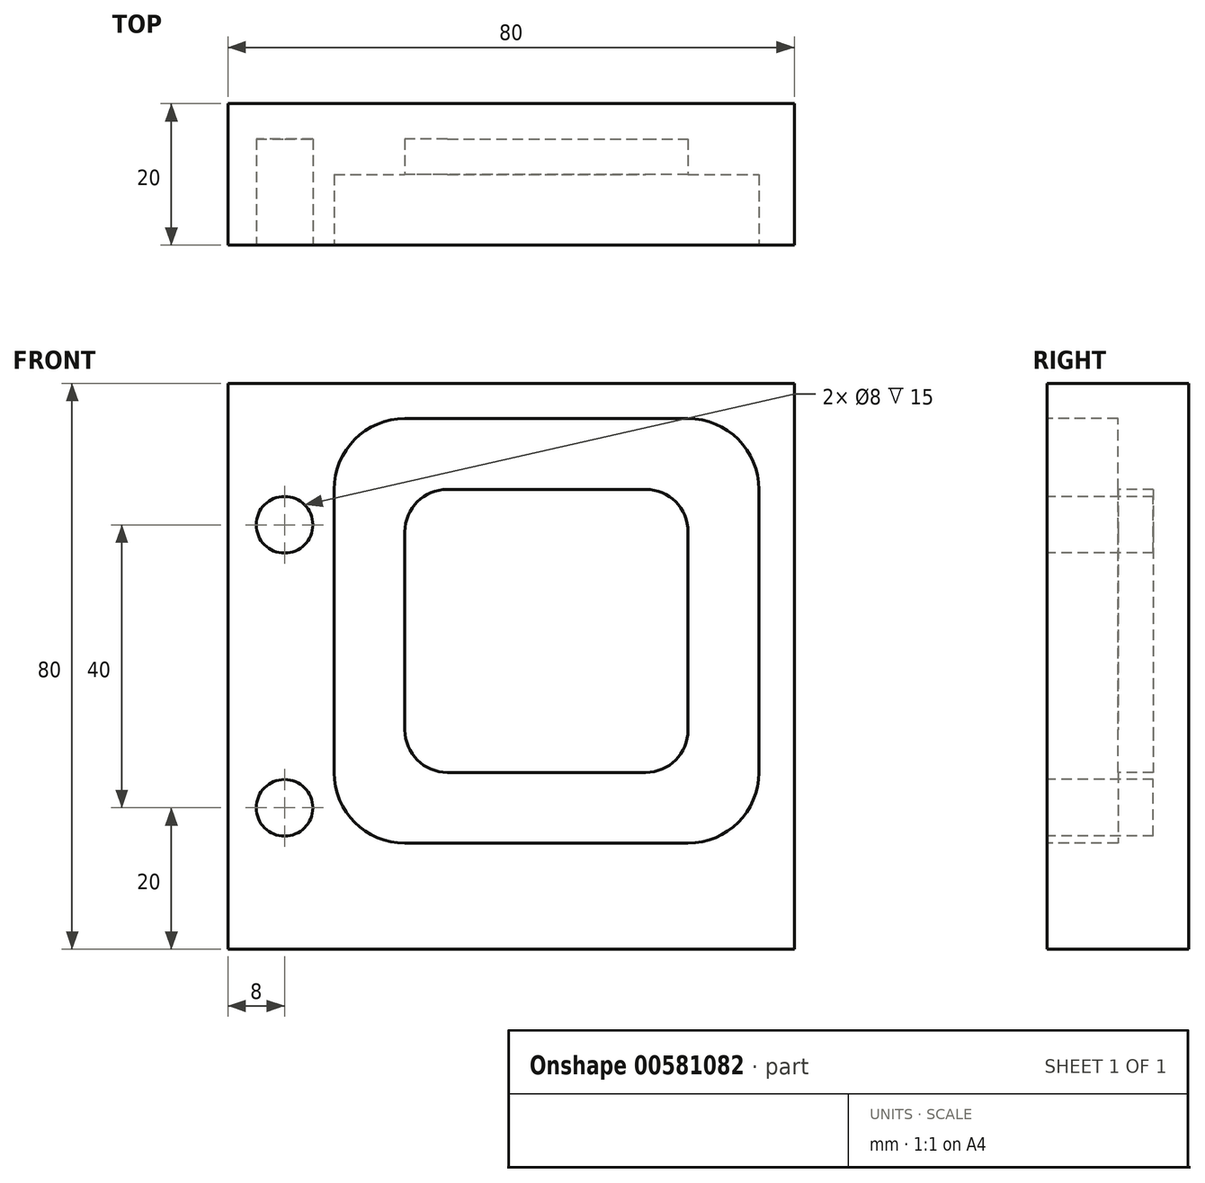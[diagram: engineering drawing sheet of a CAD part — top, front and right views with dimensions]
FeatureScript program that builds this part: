
annotation { "Feature Type Name" : "Feature", "Feature Type Description" : "" }
export const myFeature = defineFeature(function(context is Context, id is Id, definition is map)
    precondition{}
    {
        {
            var Q0;
            Q0=qCreatedBy(makeId("Front.planeOp"),FACE);
            var sketch = newSketch(context, id + "F0", { "sketchPlane" : qUnion([Q0])});
            skLineSegment(sketch, "E0.bottom", {"start": v(-40, 40) * mm, "end": v(40, 40) * mm});
            skLineSegment(sketch, "E0.top", {"start": v(-40, -40) * mm, "end": v(40, -40) * mm});
            skLineSegment(sketch, "E0.left", {"start": v(-40, 40) * mm, "end": v(-40, -40) * mm});
            skLineSegment(sketch, "E0.right", {"start": v(40, 40) * mm, "end": v(40, -40) * mm});
            skPoint(sketch, "E0.middle", {"position": v(0, 0) * mm});
            skSolve(sketch);
        }
        {
            var Q0;
            Q0=makeQuery(id+"F0.imprint","IMPRINT",FACE,{"disambiguationData":[TD([[makeQuery(id+"F0.imprint","IMPRINT",EDGE,{"derivedFrom":sQuery(id+"F0.wireOp",EDGE,"E0.bottom")}),-1.0]])]});
            extrude(context, id + "F1", {"entities" : qUnion([Q0]), "depth" : 20 * mm, "offsetDistance" : 25 * mm});
        }
        {
            var Q0;
            Q0=makeQuery(id+"F1.opExtrude","CAP_FACE",FACE,{"disambiguationData":[OSD([sQuery(id+"F0.wireOp",EDGE,"E0.bottom"),sQuery(id+"F0.wireOp",EDGE,"E0.top"),sQuery(id+"F0.wireOp",EDGE,"E0.left"),sQuery(id+"F0.wireOp",EDGE,"E0.right")])],"isStart":false});
            var sketch = newSketch(context, id + "F2", { "sketchPlane" : qUnion([Q0])});
            skCircle(sketch, "E1", {"center": v(-32, 20) * mm, "radius": 4 * mm});
            skCircle(sketch, "E2", {"center": v(-32, -20) * mm, "radius": 4 * mm});
            skSolve(sketch);
        }
        {
            var Q0;
            Q0=makeQuery(id+"F2.imprint","IMPRINT",FACE,{"disambiguationData":[TD([[makeQuery(id+"F2.imprint","IMPRINT",EDGE,{"derivedFrom":sQuery(id+"F2.wireOp",EDGE,"E1")}),1.0]])]});
            var Q1;
            Q1=makeQuery(id+"F2.imprint","IMPRINT",FACE,{"disambiguationData":[TD([[makeQuery(id+"F2.imprint","IMPRINT",EDGE,{"derivedFrom":sQuery(id+"F2.wireOp",EDGE,"E2")}),1.0]])]});
            extrude(context, id + "F3", {"entities" : qUnion([Q0, Q1]), "operationType" : NewBodyOperationType.REMOVE, "oppositeDirection" : true, "depth" : 15 * mm, "offsetDistance" : 25 * mm});
        }
        {
            var Q0;
            Q0=makeQuery(id+"F1.opExtrude","CAP_FACE",FACE,{"disambiguationData":[OSD([sQuery(id+"F0.wireOp",EDGE,"E0.bottom"),sQuery(id+"F0.wireOp",EDGE,"E0.top"),sQuery(id+"F0.wireOp",EDGE,"E0.left"),sQuery(id+"F0.wireOp",EDGE,"E0.right")])],"isStart":false});
            var sketch = newSketch(context, id + "F4", { "sketchPlane" : qUnion([Q0])});
            skLineSegment(sketch, "E3.bottom", {"start": v(25, -25) * mm, "end": v(-15, -25) * mm});
            skLineSegment(sketch, "E3.top", {"start": v(25, 35) * mm, "end": v(-15, 35) * mm});
            skLineSegment(sketch, "E3.left", {"start": v(35, -15) * mm, "end": v(35, 25) * mm});
            skLineSegment(sketch, "E3.right", {"start": v(-25, -15) * mm, "end": v(-25, 25) * mm});
            skPoint(sketch, "E3.middle", {"position": v(5, 5) * mm});
            skPoint(sketch, "E4.visualSharp", {"position": v(-25, 35) * mm});
            skArc(sketch, "E4.filletArc", {"start": v(-15, 35) * mm, "mid": v(-22.07, 32.07) * mm, "end": v(-25, 25) * mm});
            skPoint(sketch, "E5.visualSharp", {"position": v(-25, -25) * mm});
            skArc(sketch, "E5.filletArc", {"start": v(-25, -15) * mm, "mid": v(-22.07, -22.07) * mm, "end": v(-15, -25) * mm});
            skPoint(sketch, "E6.visualSharp", {"position": v(35, -25) * mm});
            skArc(sketch, "E6.filletArc", {"start": v(25, -25) * mm, "mid": v(32.07, -22.07) * mm, "end": v(35, -15) * mm});
            skPoint(sketch, "E7.visualSharp", {"position": v(35, 35) * mm});
            skArc(sketch, "E7.filletArc", {"start": v(35, 25) * mm, "mid": v(32.07, 32.07) * mm, "end": v(25, 35) * mm});
            skSolve(sketch);
        }
        {
            var Q0;
            Q0=makeQuery(id+"F4.imprint","IMPRINT",FACE,{"disambiguationData":[TD([[makeQuery(id+"F4.imprint","IMPRINT",EDGE,{"derivedFrom":sQuery(id+"F4.wireOp",EDGE,"E3.bottom")}),-1.0]])]});
            extrude(context, id + "F5", {"entities" : qUnion([Q0]), "operationType" : NewBodyOperationType.REMOVE, "oppositeDirection" : true, "depth" : 10 * mm, "offsetDistance" : 25 * mm});
        }
        {
            var Q0;
            Q0=makeQuery(id+"F5.boolean.opBoolean","COPY",FACE,{"derivedFrom":makeQuery(id+"F5.opExtrude","CAP_FACE",FACE,{"disambiguationData":[OSD([sQuery(id+"F4.wireOp",EDGE,"E3.bottom"),sQuery(id+"F4.wireOp",EDGE,"E3.top"),sQuery(id+"F4.wireOp",EDGE,"E3.left"),sQuery(id+"F4.wireOp",EDGE,"E3.right"),sQuery(id+"F4.wireOp",EDGE,"E4.filletArc"),sQuery(id+"F4.wireOp",EDGE,"E5.filletArc"),sQuery(id+"F4.wireOp",EDGE,"E6.filletArc"),sQuery(id+"F4.wireOp",EDGE,"E7.filletArc")])],"isStart":false})});
            var sketch = newSketch(context, id + "F6", { "sketchPlane" : qUnion([Q0])});
            skLineSegment(sketch, "E8.bottom", {"start": v(-9, 25) * mm, "end": v(19, 25) * mm});
            skLineSegment(sketch, "E8.top", {"start": v(-9, -15) * mm, "end": v(19, -15) * mm});
            skLineSegment(sketch, "E8.left", {"start": v(-15, 19) * mm, "end": v(-15, -9) * mm});
            skLineSegment(sketch, "E8.right", {"start": v(25, 19) * mm, "end": v(25, -9) * mm});
            skPoint(sketch, "E8.middle", {"position": v(5, 5) * mm});
            skPoint(sketch, "E9.visualSharp", {"position": v(25, 25) * mm});
            skArc(sketch, "E9.filletArc", {"start": v(25, 19) * mm, "mid": v(23.24, 23.24) * mm, "end": v(19, 25) * mm});
            skPoint(sketch, "E10.visualSharp", {"position": v(-15, 25) * mm});
            skArc(sketch, "E10.filletArc", {"start": v(-9, 25) * mm, "mid": v(-13.24, 23.24) * mm, "end": v(-15, 19) * mm});
            skPoint(sketch, "E11.visualSharp", {"position": v(-15, -15) * mm});
            skArc(sketch, "E11.filletArc", {"start": v(-15, -9) * mm, "mid": v(-13.24, -13.24) * mm, "end": v(-9, -15) * mm});
            skPoint(sketch, "E12.visualSharp", {"position": v(25, -15) * mm});
            skArc(sketch, "E12.filletArc", {"start": v(19, -15) * mm, "mid": v(23.24, -13.24) * mm, "end": v(25, -9) * mm});
            skSolve(sketch);
        }
        {
            var Q0;
            Q0=makeQuery(id+"F6.imprint","IMPRINT",FACE,{"disambiguationData":[TD([[makeQuery(id+"F6.imprint","IMPRINT",EDGE,{"derivedFrom":sQuery(id+"F6.wireOp",EDGE,"E8.bottom")}),-1.0]])]});
            extrude(context, id + "F7", {"entities" : qUnion([Q0]), "operationType" : NewBodyOperationType.REMOVE, "oppositeDirection" : true, "depth" : 5 * mm, "offsetDistance" : 25 * mm});
        }
    });
